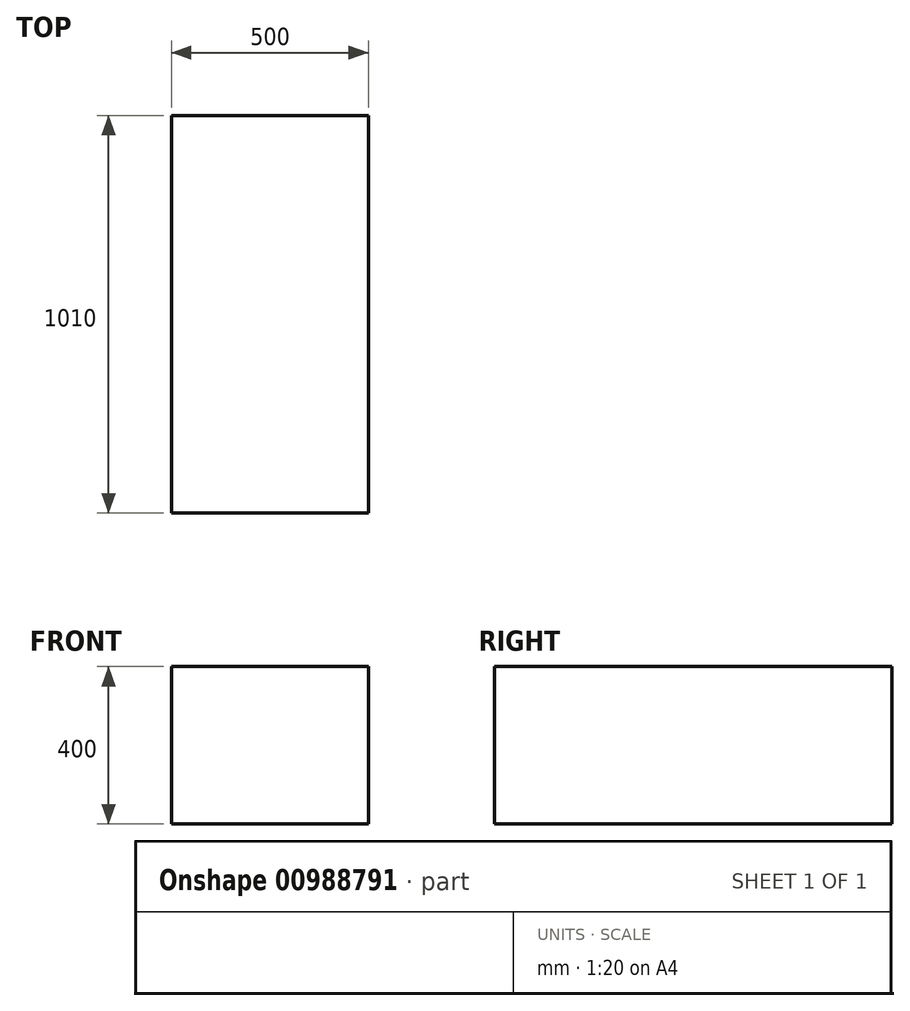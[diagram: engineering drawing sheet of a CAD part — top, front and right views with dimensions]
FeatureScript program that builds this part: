
annotation { "Feature Type Name" : "Feature", "Feature Type Description" : "" }
export const myFeature = defineFeature(function(context is Context, id is Id, definition is map)
    precondition{}
    {
        {
            var Q0;
            Q0=qCreatedBy(makeId("Front.planeOp"),FACE);
            var sketch = newSketch(context, id + "F0", { "sketchPlane" : qUnion([Q0])});
            skLineSegment(sketch, "E0.bottom", {"start": v(250, 200) * mm, "end": v(-250, 200) * mm});
            skLineSegment(sketch, "E0.top", {"start": v(250, -200) * mm, "end": v(-250, -200) * mm});
            skLineSegment(sketch, "E0.left", {"start": v(250, 200) * mm, "end": v(250, -200) * mm});
            skLineSegment(sketch, "E0.right", {"start": v(-250, 200) * mm, "end": v(-250, -200) * mm});
            skPoint(sketch, "E0.middle", {"position": v(0, 0) * mm});
            skSolve(sketch);
        }
        {
            var Q0;
            Q0=makeQuery(id+"F0.imprint","IMPRINT",FACE,{"disambiguationData":[TD([[makeQuery(id+"F0.imprint","IMPRINT",EDGE,{"derivedFrom":sQuery(id+"F0.wireOp",EDGE,"E0.bottom")}),1.0]])]});
            extrude(context, id + "F1", {"entities" : qUnion([Q0]), "depth" : 1010 * mm, "offsetDistance" : 25 * mm});
        }
    });
